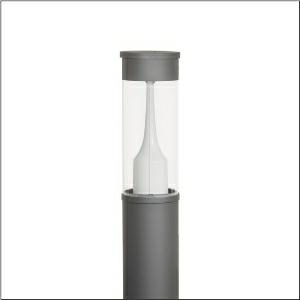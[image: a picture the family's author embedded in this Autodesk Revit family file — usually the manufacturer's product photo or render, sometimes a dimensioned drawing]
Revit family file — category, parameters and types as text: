
# Revit family: city-light_260_iq___p1_0a_5xa5295nf14h_1e18
name_source: partatom
category: Lighting Fixtures
units: mm (PartAtom-declared; Revit-internal decimal feet)

## family parameters
Cut with Voids When Loaded = No
Host = Face
Light Source = No
Part Type = Normal
Room Calculation Point = No
Round Connector Dimension = Use Diameter
Shared = No

## types (1)
- --- (1 x LED, 1510 lm, 11.8 W, 2700K)
    Apparent Load = 12 VA
    CIE Flux Codes = 32 61 90 93 100
    Color Rendering = 70
    Color Temperature = 2700K
    Default Elevation = 1800 mm
    Description = City-Light 260 iQ, light pillar, Module 540 iQ-SR, primary light control with 3 zone facetted reflector, of plastic, silver coated, highly specular, structured, primary optical cover: cover, of PMMA, transparent, partly coated, light distribution: P1.0a, primary light characteristic: strongly asymmetric, LED, High Power LED, rated luminous flux: 1.510lm, luminous efficacy: 128lm/W, light colour: 727, colour temperature: 2700K, control gear: iQ Street-Remote, control: pre-setting: logarithmic dimming characteristic, Street-Remote, Auto-Match, Temp-Guard, Lumen-Switch, Night-Set, Smart-Wire, Light-Fading, Desk-Remote (wireless, voltage-free reading and setting of iQ features in the workshop via application-optimized NFC function/RFID function), optimised constant luminous flux control (CLO 2.0), with terminal, 6-pole, max. 2.5mm², mains connection: 230..240V, AC, 50/60Hz, start of lifetime: 12W, end of service life: 12W, reduction: 6W, luminaire housing, cylindrical, of extruded aluminium section, coated, Siteco® metallic grey (DB 702S), length: 2.600mm, diameter: 200mm, Module 540 iQ-SR, traffic white (RAL 9016), equipment: standard, protection rating (complete): IP65, insulation class (complete): insulation class II (safety insulation), certification: CE, ENEC, VDE, packaging unit: 1 piece

Light Distribution: P1.0a
    Height = 500 mm
    Lamp = 1 x LED
    Lamp Light Flux = 1510 lm
    Lamp Power = 11.8 W
    Lamp count = 1
    Length = 200 mm  [stored 0.656168 ft]
    Luminous efficacy = 128 lm/W
    Manufacturer = Siteco
    ModVariant = No
    Model = 5XA5295NF14H
    Mounting Place = Floor
    Mounting Type = Freestanding
    Number of Poles = 1
    OnlyDefault = Yes
    Power Factor = 1
    Product Name = City-Light 260 iQ | P1.0a
    Product group = light pillar
    ProductGroupID = 1301
    Protection Class = Protection class II
    Protection Degree = IP 65
    RLX_Detail_Level = 1
    RLX_Emergency_Light_Flux = 0 lm
    RLX_Emergency_Type = 0
    RLX_Emergency_Type_DB = No
    RlxData = <blob elided: 52569 chars, md5=2c43c9d6>
    Socket = socket
    Standby Power = 0 W
    System Light Flux = 1510 lm
    System Power = 12 W
    Type Comments = factory setting: luminous flux: 100 % | dim-lin: 254 | 472 mA
    Type Image = l_1006918.jpg
    URL = http://relux.com
    VarID = @adj_152643
    Voltage = 0 V
    Weight = 0.00 kg
    Width = 0 mm  [stored 0 ft]

note: [stored X ft] marks values corroborated as IEEE doubles in the binary element streams (Revit-internal decimal feet)

## geometry (parser evidence)
native form markers: Blend x4, Sweep x10
no freeform markers — native parametric forms only
